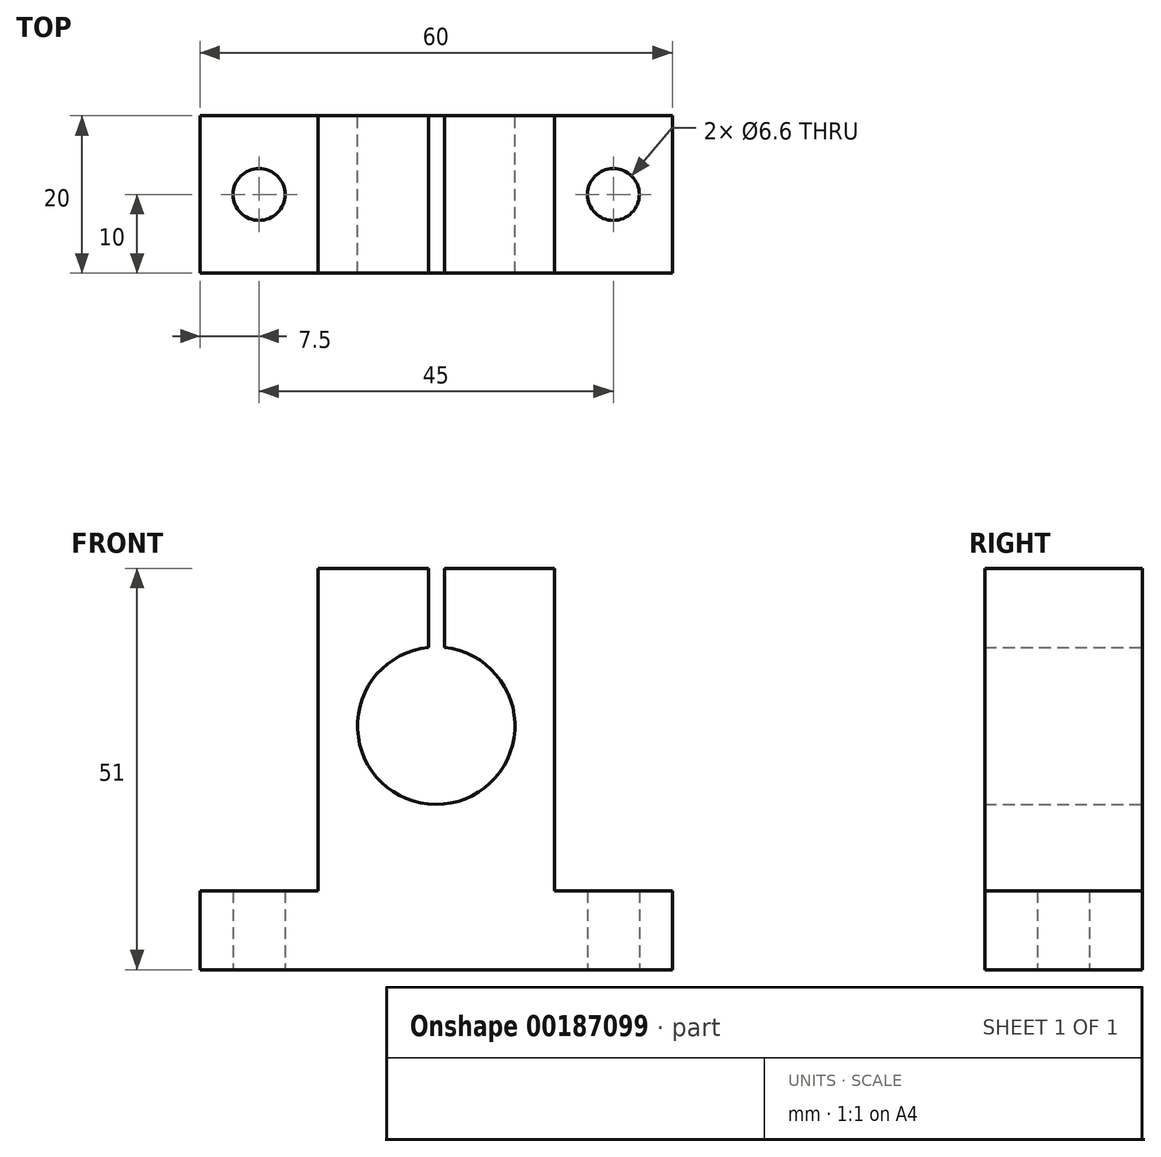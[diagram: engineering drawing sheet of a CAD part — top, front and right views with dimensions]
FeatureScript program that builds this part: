
annotation { "Feature Type Name" : "Feature", "Feature Type Description" : "" }
export const myFeature = defineFeature(function(context is Context, id is Id, definition is map)
    precondition{}
    {
        {
            var Q0;
            Q0=qCreatedBy(makeId("Front.planeOp"),FACE);
            var sketch = newSketch(context, id + "F0", { "sketchPlane" : qUnion([Q0])});
            skLineSegment(sketch, "E0.bottom", {"start": v(30, -25.5) * mm, "end": v(-30, -25.5) * mm});
            skLineSegment(sketch, "E0.top", {"start": v(15, 25.5) * mm, "end": v(1.06, 25.5) * mm});
            skLineSegment(sketch, "E0.left", {"start": v(30, -25.5) * mm, "end": v(30, -15.5) * mm});
            skLineSegment(sketch, "E0.right", {"start": v(-30, -25.5) * mm, "end": v(-30, -15.5) * mm});
            skPoint(sketch, "E0.middle", {"position": v(0, 0) * mm});
            skLineSegment(sketch, "E1", {"start": v(-15, 25.5) * mm, "end": v(-15, -10.49) * mm});
            skLineSegment(sketch, "E2", {"start": v(15, 25.5) * mm, "end": v(15, -15.5) * mm});
            skLineSegment(sketch, "E3", {"start": v(-30, -15.5) * mm, "end": v(-15, -15.5) * mm});
            skArc(sketch, "E4", {"start": v(-0.95, 15.45) * mm, "mid": v(-0.05, -4.5) * mm, "end": v(1.06, 15.44) * mm});
            skLineSegment(sketch, "E5", {"start": v(-0.95, 25.5) * mm, "end": v(-0.95, 15.45) * mm});
            skLineSegment(sketch, "E6", {"start": v(1.06, 25.5) * mm, "end": v(1.06, 15.44) * mm});
            skPoint(sketch, "E7.orphan", {"position": v(-30, 25.5) * mm});
            skLineSegment(sketch, "E8.trimOffspring", {"start": v(-0.95, 25.5) * mm, "end": v(-15, 25.5) * mm});
            skPoint(sketch, "E9.orphan", {"position": v(30, 25.5) * mm});
            skPoint(sketch, "E10.orphan", {"position": v(30, 5.5) * mm});
            skPoint(sketch, "E11.orphan", {"position": v(-30, 5.5) * mm});
            skLineSegment(sketch, "E12.trimOffspring", {"start": v(15, -15.5) * mm, "end": v(30, -15.5) * mm});
            skLineSegment(sketch, "E13", {"start": v(-15, -10.49) * mm, "end": v(-15, -15.5) * mm});
            skSolve(sketch);
        }
        {
            var Q0;
            Q0=makeQuery(id+"F0.imprint","IMPRINT",FACE,{"disambiguationData":[TD([[makeQuery(id+"F0.imprint","IMPRINT",EDGE,{"derivedFrom":sQuery(id+"F0.wireOp",EDGE,"E0.bottom")}),-1.0]])]});
            extrude(context, id + "F1", {"entities" : qUnion([Q0]), "depth" : 20 * mm});
        }
        {
            var Q0;
            Q0=makeQuery(id+"F1.opExtrude","SWEPT_FACE",FACE,{"disambiguationData":[OSD([sQuery(id+"F0.wireOp",EDGE,"E0.bottom")])]});
            var sketch = newSketch(context, id + "F2", { "sketchPlane" : qUnion([Q0])});
            skArc(sketch, "E14", {"start": v(-19.84, 8.05) * mm, "mid": v(-25.1, 12.02) * mm, "end": v(-19.94, 7.91) * mm});
            skCircle(sketch, "E15", {"center": v(22.5, 10) * mm, "radius": 3.3 * mm});
            skPoint(sketch, "E16.orphan", {"position": v(-22.5, 20) * mm});
            skPoint(sketch, "E17.orphan", {"position": v(-30, 10) * mm});
            skPoint(sketch, "E18.orphan", {"position": v(-22.5, 0) * mm});
            skPoint(sketch, "E19.orphan", {"position": v(22.5, 0) * mm});
            skPoint(sketch, "E20.orphan", {"position": v(30, 10) * mm});
            skPoint(sketch, "E21.orphan", {"position": v(22.5, 20) * mm});
            skPoint(sketch, "E22.orphan", {"position": v(-17.5, 20) * mm});
            skPoint(sketch, "E23.start.orphan", {"position": v(-17.5, 0) * mm});
            skSolve(sketch);
        }
        {
            var Q0;
            Q0=sQuery(id+"F2.wireOp",VERTEX,"E14.center");
            var Q1;
            Q1=makeQuery(id+"F1.opExtrude","SWEPT_BODY",BODY,{"disambiguationData":[OSD([sQuery(id+"F0.wireOp",EDGE,"E0.bottom"),sQuery(id+"F0.wireOp",EDGE,"E0.top"),sQuery(id+"F0.wireOp",EDGE,"E0.left"),sQuery(id+"F0.wireOp",EDGE,"E0.right"),sQuery(id+"F0.wireOp",EDGE,"E1"),sQuery(id+"F0.wireOp",EDGE,"E2"),sQuery(id+"F0.wireOp",EDGE,"E3"),sQuery(id+"F0.wireOp",EDGE,"E4"),sQuery(id+"F0.wireOp",EDGE,"E5"),sQuery(id+"F0.wireOp",EDGE,"E6"),sQuery(id+"F0.wireOp",EDGE,"E8.trimOffspring"),sQuery(id+"F0.wireOp",EDGE,"E12.trimOffspring")])]});
            hole(context, id + "F3", {"style" : HoleStyle.SIMPLE, "endStyle" : HoleEndStyle.THROUGH, "holeDiameter" : 6.6 * mm, "locations" : qUnion([Q0]), "scope" : qUnion([Q1]), "isTappedThrough" : true});
        }
        {
            var Q0;
            Q0=sQuery(id+"F2.wireOp",VERTEX,"E15.center");
            var Q1;
            Q1=makeQuery(id+"F1.opExtrude","SWEPT_BODY",BODY,{"disambiguationData":[OSD([sQuery(id+"F0.wireOp",EDGE,"E0.bottom"),sQuery(id+"F0.wireOp",EDGE,"E0.top"),sQuery(id+"F0.wireOp",EDGE,"E0.left"),sQuery(id+"F0.wireOp",EDGE,"E0.right"),sQuery(id+"F0.wireOp",EDGE,"E1"),sQuery(id+"F0.wireOp",EDGE,"E2"),sQuery(id+"F0.wireOp",EDGE,"E3"),sQuery(id+"F0.wireOp",EDGE,"E4"),sQuery(id+"F0.wireOp",EDGE,"E5"),sQuery(id+"F0.wireOp",EDGE,"E6"),sQuery(id+"F0.wireOp",EDGE,"E8.trimOffspring"),sQuery(id+"F0.wireOp",EDGE,"E12.trimOffspring")])]});
            hole(context, id + "F4", {"style" : HoleStyle.SIMPLE, "endStyle" : HoleEndStyle.THROUGH, "holeDiameter" : 6.6 * mm, "locations" : qUnion([Q0]), "scope" : qUnion([Q1]), "isTappedThrough" : true});
        }
    });
